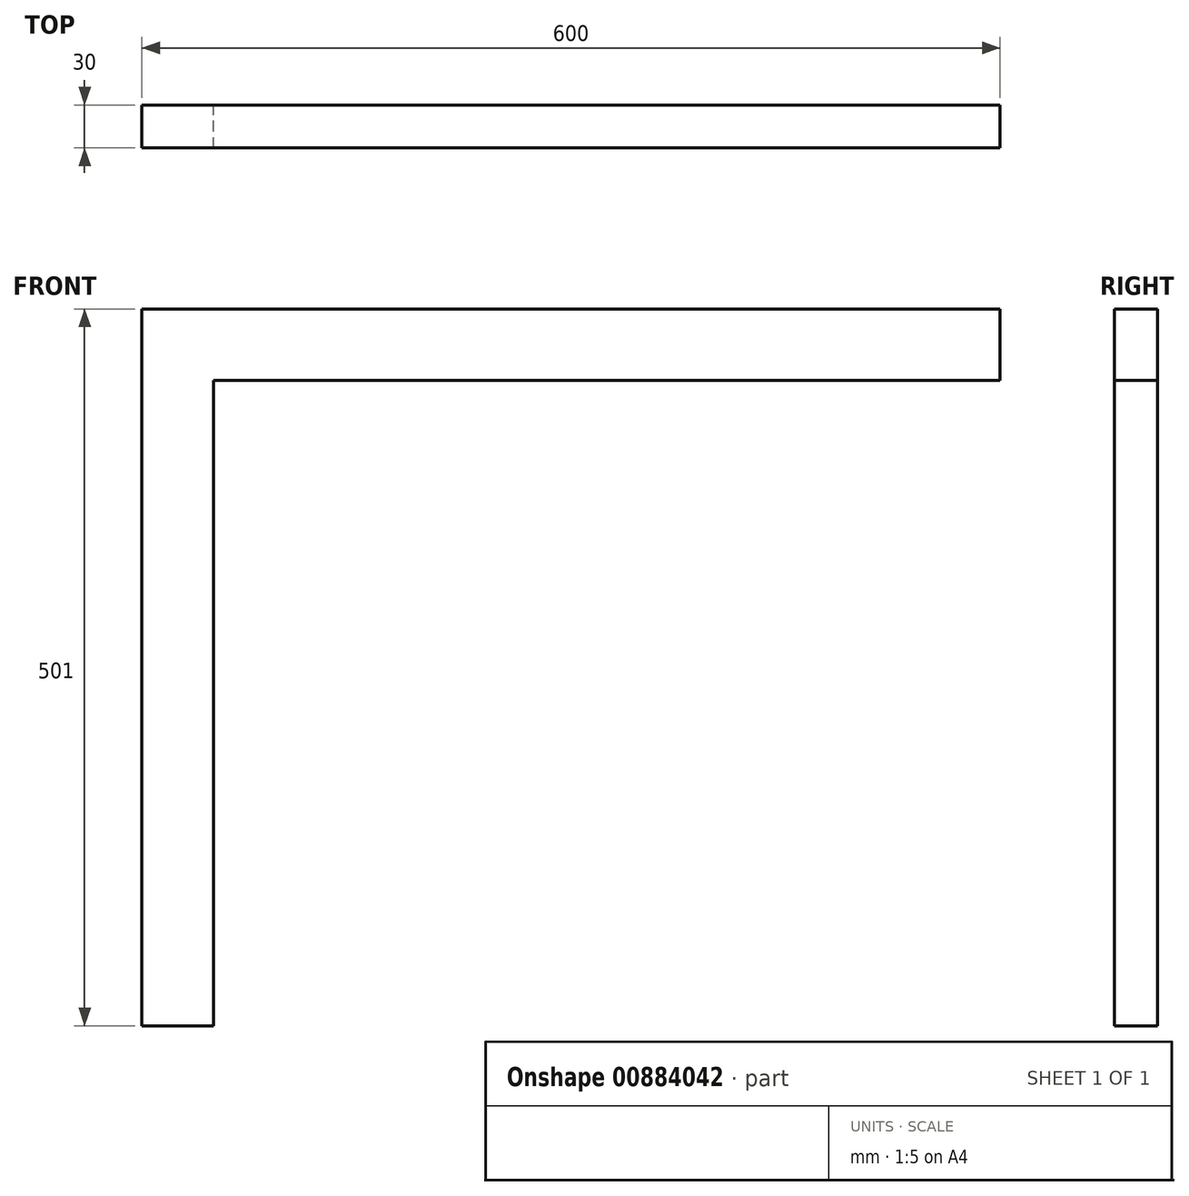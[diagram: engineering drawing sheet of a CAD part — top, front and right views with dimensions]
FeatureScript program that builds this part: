
annotation { "Feature Type Name" : "Feature", "Feature Type Description" : "" }
export const myFeature = defineFeature(function(context is Context, id is Id, definition is map)
    precondition{}
    {
        {
            var Q0;
            Q0=qCreatedBy(makeId("Front.planeOp"),FACE);
            var sketch = newSketch(context, id + "F0", { "sketchPlane" : qUnion([Q0])});
            skLineSegment(sketch, "E0.bottom", {"start": v(0, 0) * mm, "end": v(50, 0) * mm});
            skLineSegment(sketch, "E0.top", {"start": v(0, -501) * mm, "end": v(50, -501) * mm});
            skLineSegment(sketch, "E0.left", {"start": v(0, 0) * mm, "end": v(0, -501) * mm});
            skLineSegment(sketch, "E0.right", {"start": v(50, 0) * mm, "end": v(50, -501) * mm});
            skLineSegment(sketch, "E1.bottom", {"start": v(0, 0) * mm, "end": v(600, 0) * mm});
            skLineSegment(sketch, "E1.top", {"start": v(0, -50) * mm, "end": v(600, -50) * mm});
            skLineSegment(sketch, "E1.left", {"start": v(0, 0) * mm, "end": v(0, -50) * mm});
            skLineSegment(sketch, "E1.right", {"start": v(600, 0) * mm, "end": v(600, -50) * mm});
            skSolve(sketch);
        }
        {
            var Q0;
            Q0=qSketchRegion(id+"F0",true);
            extrude(context, id + "F1", {"entities" : qUnion([Q0]), "depth" : 30 * mm, "offsetDistance" : 25 * mm});
        }
    });
